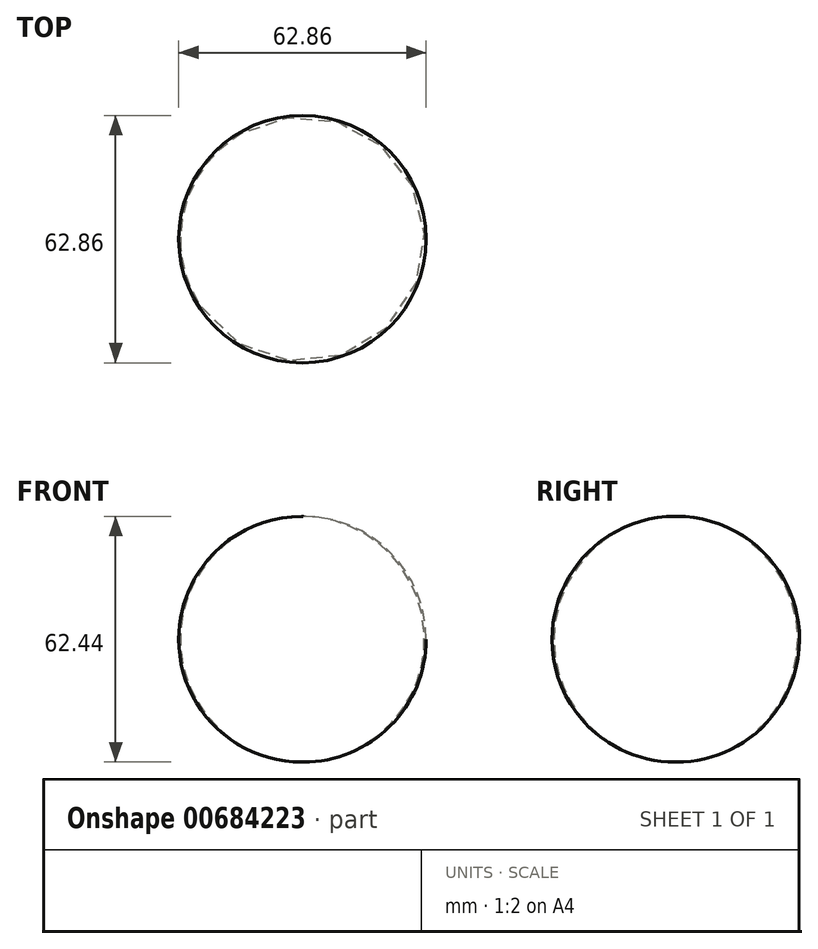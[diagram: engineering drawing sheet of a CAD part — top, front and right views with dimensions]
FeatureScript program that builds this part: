
annotation { "Feature Type Name" : "Feature", "Feature Type Description" : "" }
export const myFeature = defineFeature(function(context is Context, id is Id, definition is map)
    precondition{}
    {
        {
            var Q0;
            Q0=qCreatedBy(makeId("Front.planeOp"),FACE);
            var sketch = newSketch(context, id + "F0", { "sketchPlane" : qUnion([Q0])});
            skArc(sketch, "E0", {"start": v(-16.17, -7.82) * mm, "mid": v(15.26, 23.4) * mm, "end": v(-16.17, 54.62) * mm});
            skLineSegment(sketch, "E1", {"start": v(-16.17, 54.62) * mm, "end": v(-16.17, -7.82) * mm});
            skSolve(sketch);
        }
        {
            var Q0;
            Q0=makeQuery(id+"F0.imprint","IMPRINT",FACE,{"disambiguationData":[TD([[makeQuery(id+"F0.imprint","IMPRINT",EDGE,{"derivedFrom":sQuery(id+"F0.wireOp",EDGE,"E0")}),1.0]])]});
            var Q1;
            Q1=sQuery(id+"F0.wireOp",EDGE,"E1");
            revolve(context, id + "F1", {"entities" : qUnion([Q0]), "axis" : qUnion([Q1]), "revolveType" : RevolveType.FULL});
        }
    });
